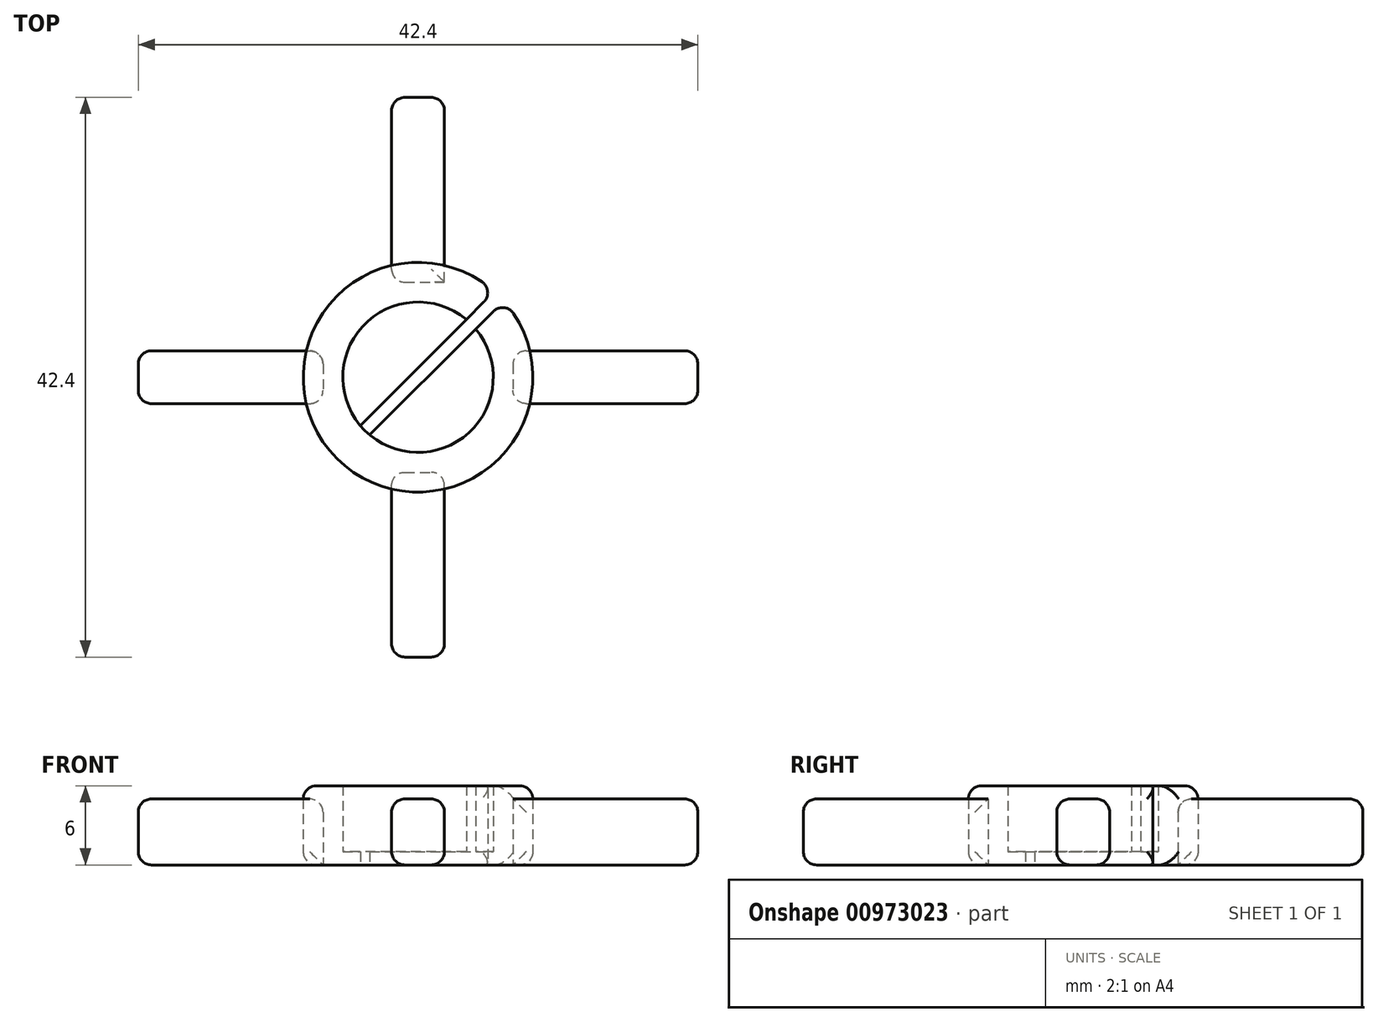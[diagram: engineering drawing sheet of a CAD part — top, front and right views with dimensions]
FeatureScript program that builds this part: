
annotation { "Feature Type Name" : "Feature", "Feature Type Description" : "" }
export const myFeature = defineFeature(function(context is Context, id is Id, definition is map)
    precondition{}
    {
        {
            var Q0;
            Q0=qCreatedBy(makeId("Top.planeOp"),FACE);
            var sketch = newSketch(context, id + "F0", { "sketchPlane" : qUnion([Q0])});
            skCircle(sketch, "E0", {"center": v(0, 0) * mm, "radius": 5.7 * mm});
            skCircle(sketch, "E1", {"center": v(0, 0) * mm, "radius": 8.7 * mm});
            skLineSegment(sketch, "E2.bottom", {"start": v(-21.2, 2) * mm, "end": v(-7.2, 2) * mm});
            skLineSegment(sketch, "E2.top", {"start": v(-21.2, -2) * mm, "end": v(-7.2, -2) * mm});
            skLineSegment(sketch, "E2.left", {"start": v(-21.2, 2) * mm, "end": v(-21.2, -2) * mm});
            skLineSegment(sketch, "E2.right", {"start": v(-7.2, 2) * mm, "end": v(-7.2, -2) * mm});
            skCircle(sketch, "E3", {"center": v(0, 0) * mm, "radius": 7.2 * mm, "construction": true});
            skPoint(sketch, "E4", {"position": v(-7.2, 0) * mm});
            skPoint(sketch, "E5", {"position": v(0, 7.2) * mm});
            skPoint(sketch, "E6", {"position": v(7.2, 0) * mm});
            skPoint(sketch, "E7", {"position": v(0, -7.2) * mm});
            skLineSegment(sketch, "E8.bottom", {"start": v(-2, 7.2) * mm, "end": v(-2, 21.2) * mm});
            skLineSegment(sketch, "E8.top", {"start": v(2, 7.2) * mm, "end": v(2, 21.2) * mm});
            skLineSegment(sketch, "E8.left", {"start": v(-2, 7.2) * mm, "end": v(2, 7.2) * mm});
            skLineSegment(sketch, "E8.right", {"start": v(-2, 21.2) * mm, "end": v(2, 21.2) * mm});
            skPoint(sketch, "E9", {"position": v(0, 21.2) * mm});
            skLineSegment(sketch, "E10.bottom", {"start": v(7.2, 2) * mm, "end": v(21.2, 2) * mm});
            skLineSegment(sketch, "E10.top", {"start": v(7.2, -2) * mm, "end": v(21.2, -2) * mm});
            skLineSegment(sketch, "E10.left", {"start": v(7.2, 2) * mm, "end": v(7.2, -2) * mm});
            skLineSegment(sketch, "E10.right", {"start": v(21.2, 2) * mm, "end": v(21.2, -2) * mm});
            skPoint(sketch, "E11", {"position": v(21.2, 0) * mm});
            skLineSegment(sketch, "E12.bottom", {"start": v(-2, -21.2) * mm, "end": v(-2, -7.2) * mm});
            skLineSegment(sketch, "E12.top", {"start": v(2, -21.2) * mm, "end": v(2, -7.2) * mm});
            skLineSegment(sketch, "E12.left", {"start": v(-2, -21.2) * mm, "end": v(2, -21.2) * mm});
            skLineSegment(sketch, "E12.right", {"start": v(-2, -7.2) * mm, "end": v(2, -7.2) * mm});
            skLineSegment(sketch, "E13.bottom", {"start": v(-0.35, 0.35) * mm, "end": v(0.35, -0.35) * mm});
            skLineSegment(sketch, "E13.top", {"start": v(13.79, 14.5) * mm, "end": v(14.5, 13.79) * mm});
            skLineSegment(sketch, "E13.left", {"start": v(-0.35, 0.35) * mm, "end": v(13.79, 14.5) * mm});
            skLineSegment(sketch, "E13.right", {"start": v(0.35, -0.35) * mm, "end": v(14.5, 13.79) * mm});
            skLineSegment(sketch, "E14", {"start": v(-0.35, 0.35) * mm, "end": v(-4.37, -3.66) * mm});
            skLineSegment(sketch, "E15", {"start": v(0.35, -0.35) * mm, "end": v(-3.66, -4.37) * mm});
            skSolve(sketch);
        }
        {
            var Q0;
            {var subQ5=sQuery(id+"F0.wireOp",EDGE,"E2.right");Q0=makeQuery(id+"F0.imprint","IMPRINT",FACE,{"disambiguationData":[TD([[makeQuery(id+"F0.imprint","IMPRINT",EDGE,{"derivedFrom":subQ5}),-1.0]])]});}
            var Q1;
            {var subQ5=sQuery(id+"F0.wireOp",EDGE,"E8.left");Q1=makeQuery(id+"F0.imprint","IMPRINT",FACE,{"disambiguationData":[TD([[makeQuery(id+"F0.imprint","IMPRINT",EDGE,{"derivedFrom":subQ5}),1.0]])]});}
            var Q2;
            {var subQ5=sQuery(id+"F0.wireOp",EDGE,"E12.left");Q2=makeQuery(id+"F0.imprint","IMPRINT",FACE,{"disambiguationData":[TD([[makeQuery(id+"F0.imprint","IMPRINT",EDGE,{"derivedFrom":subQ5}),1.0]])]});}
            var Q3;
            {var subQ5=sQuery(id+"F0.wireOp",EDGE,"E12.right");Q3=makeQuery(id+"F0.imprint","IMPRINT",FACE,{"disambiguationData":[TD([[makeQuery(id+"F0.imprint","IMPRINT",EDGE,{"derivedFrom":subQ5}),-1.0]])]});}
            var Q4;
            {var subQ5=sQuery(id+"F0.wireOp",EDGE,"E10.right");Q4=makeQuery(id+"F0.imprint","IMPRINT",FACE,{"disambiguationData":[TD([[makeQuery(id+"F0.imprint","IMPRINT",EDGE,{"derivedFrom":subQ5}),-1.0]])]});}
            var Q5;
            {var subQ5=sQuery(id+"F0.wireOp",EDGE,"E10.left");Q5=makeQuery(id+"F0.imprint","IMPRINT",FACE,{"disambiguationData":[TD([[makeQuery(id+"F0.imprint","IMPRINT",EDGE,{"derivedFrom":subQ5}),1.0]])]});}
            var Q6;
            {var subQ5=sQuery(id+"F0.wireOp",EDGE,"E2.left");Q6=makeQuery(id+"F0.imprint","IMPRINT",FACE,{"disambiguationData":[TD([[makeQuery(id+"F0.imprint","IMPRINT",EDGE,{"derivedFrom":subQ5}),1.0]])]});}
            var Q7;
            {var subQ5=sQuery(id+"F0.wireOp",EDGE,"E8.right");Q7=makeQuery(id+"F0.imprint","IMPRINT",FACE,{"disambiguationData":[TD([[makeQuery(id+"F0.imprint","IMPRINT",EDGE,{"derivedFrom":subQ5}),-1.0]])]});}
            extrude(context, id + "F1", {"entities" : qUnion([Q0, Q1, Q2, Q3, Q4, Q5, Q6, Q7]), "depth" : 5 * mm, "offsetDistance" : 25 * mm});
        }
        {
            var Q0;
            {var subQ21=sQuery(id+"F0.wireOp",EDGE,"E2.right");Q0=makeQuery(id+"F0.imprint","IMPRINT",FACE,{"disambiguationData":[TD([[makeQuery(id+"F0.imprint","IMPRINT",EDGE,{"derivedFrom":subQ21}),1.0]])]});}
            var Q1;
            {var subQ5=sQuery(id+"F0.wireOp",EDGE,"E12.right");Q1=makeQuery(id+"F0.imprint","IMPRINT",FACE,{"disambiguationData":[TD([[makeQuery(id+"F0.imprint","IMPRINT",EDGE,{"derivedFrom":subQ5}),-1.0]])]});}
            var Q2;
            {var subQ5=sQuery(id+"F0.wireOp",EDGE,"E10.left");Q2=makeQuery(id+"F0.imprint","IMPRINT",FACE,{"disambiguationData":[TD([[makeQuery(id+"F0.imprint","IMPRINT",EDGE,{"derivedFrom":subQ5}),1.0]])]});}
            var Q3;
            {var subQ5=sQuery(id+"F0.wireOp",EDGE,"E8.left");Q3=makeQuery(id+"F0.imprint","IMPRINT",FACE,{"disambiguationData":[TD([[makeQuery(id+"F0.imprint","IMPRINT",EDGE,{"derivedFrom":subQ5}),1.0]])]});}
            var Q4;
            {var subQ5=sQuery(id+"F0.wireOp",EDGE,"E2.right");Q4=makeQuery(id+"F0.imprint","IMPRINT",FACE,{"disambiguationData":[TD([[makeQuery(id+"F0.imprint","IMPRINT",EDGE,{"derivedFrom":subQ5}),-1.0]])]});}
            extrude(context, id + "F2", {"entities" : qUnion([Q0, Q1, Q2, Q3, Q4]), "depth" : 6 * mm, "offsetDistance" : 25 * mm});
        }
        {
            var Q0;
            {var subQ5=sQuery(id+"F0.wireOp",EDGE,"E13.top");Q0=makeQuery(id+"F0.imprint","IMPRINT",FACE,{"disambiguationData":[TD([[makeQuery(id+"F0.imprint","IMPRINT",EDGE,{"derivedFrom":subQ5}),-1.0]])]});}
            var Q1;
            {var subQ0=sQuery(id+"F0.wireOp",EDGE,"E13.left");var subQ1=sQuery(id+"F0.wireOp",EDGE,"E0");var subQ2=makeQuery(id+"F0.imprint","INTERSECT",VERTEX,{"derivedFrom":[subQ1,subQ0]});Q1=makeQuery(id+"F0.imprint","IMPRINT",FACE,{"disambiguationData":[TD([[makeQuery(id+"F0.imprint","IMPRINT",EDGE,{"disambiguationData":[TD([[subQ2,1.0]])],"derivedFrom":subQ1}),-1.0]])]});}
            var Q2;
            {var subQ5=sQuery(id+"F0.wireOp",EDGE,"E13.bottom");Q2=makeQuery(id+"F0.imprint","IMPRINT",FACE,{"disambiguationData":[TD([[makeQuery(id+"F0.imprint","IMPRINT",EDGE,{"derivedFrom":subQ5}),1.0]])]});}
            var Q3;
            Q3=makeQuery(id+"F0.imprint","IMPRINT",FACE,{"disambiguationData":[TD([[makeQuery(id+"F0.imprint","IMPRINT",EDGE,{"derivedFrom":sQuery(id+"F0.wireOp",EDGE,"E13.bottom")}),-1.0]])]});
            var Q4;
            Q4=makeQuery(id+"F2.opExtrude","CAP_FACE",FACE,{"disambiguationData":[OSD([sQuery(id+"F0.wireOp",EDGE,"E0"),sQuery(id+"F0.wireOp",EDGE,"E1"),sQuery(id+"F0.wireOp",EDGE,"E13.left"),sQuery(id+"F0.wireOp",EDGE,"E13.right")])],"isStart":false});
            extrude(context, id + "F3", {"entities" : qUnion([Q0, Q1, Q2, Q3]), "operationType" : NewBodyOperationType.REMOVE, "endBound" : BoundingType.UP_TO_SURFACE, "depth" : -25 * mm, "endBoundEntityFace" : qUnion([Q4]), "offsetDistance" : 25 * mm});
        }
        {
            var Q0;
            Q0=makeQuery(id+"F2.opExtrude","SWEPT_FACE",FACE,{"disambiguationData":[OSD([sQuery(id+"F0.wireOp",EDGE,"E1")])]});
            var Q1;
            Q1=makeQuery(id+"F1.opExtrude","SWEPT_FACE",FACE,{"disambiguationData":[OSD([sQuery(id+"F0.wireOp",EDGE,"E12.top")])]});
            var Q2;
            Q2=makeQuery(id+"F1.opExtrude","SWEPT_FACE",FACE,{"disambiguationData":[OSD([sQuery(id+"F0.wireOp",EDGE,"E12.bottom")])]});
            var Q3;
            Q3=makeQuery(id+"F1.opExtrude","SWEPT_FACE",FACE,{"disambiguationData":[OSD([sQuery(id+"F0.wireOp",EDGE,"E12.left")])]});
            var Q4;
            Q4=makeQuery(id+"F1.opExtrude","SWEPT_FACE",FACE,{"disambiguationData":[OSD([sQuery(id+"F0.wireOp",EDGE,"E8.bottom")])]});
            var Q5;
            Q5=makeQuery(id+"F1.opExtrude","CAP_FACE",FACE,{"disambiguationData":[OSD([sQuery(id+"F0.wireOp",EDGE,"E8.bottom"),sQuery(id+"F0.wireOp",EDGE,"E8.top"),sQuery(id+"F0.wireOp",EDGE,"E8.left"),sQuery(id+"F0.wireOp",EDGE,"E8.right")])],"isStart":false});
            var Q6;
            Q6=makeQuery(id+"F1.opExtrude","SWEPT_FACE",FACE,{"disambiguationData":[OSD([sQuery(id+"F0.wireOp",EDGE,"E8.right")])]});
            var Q7;
            Q7=makeQuery(id+"F1.opExtrude","SWEPT_FACE",FACE,{"disambiguationData":[OSD([sQuery(id+"F0.wireOp",EDGE,"E2.left")])]});
            var Q8;
            Q8=makeQuery(id+"F1.opExtrude","CAP_FACE",FACE,{"disambiguationData":[OSD([sQuery(id+"F0.wireOp",EDGE,"E2.bottom"),sQuery(id+"F0.wireOp",EDGE,"E2.top"),sQuery(id+"F0.wireOp",EDGE,"E2.left"),sQuery(id+"F0.wireOp",EDGE,"E2.right")])],"isStart":false});
            var Q9;
            Q9=makeQuery(id+"F1.opExtrude","SWEPT_FACE",FACE,{"disambiguationData":[OSD([sQuery(id+"F0.wireOp",EDGE,"E2.top")])]});
            var Q10;
            Q10=makeQuery(id+"F1.opExtrude","SWEPT_FACE",FACE,{"disambiguationData":[OSD([sQuery(id+"F0.wireOp",EDGE,"E2.bottom")])]});
            var Q11;
            Q11=makeQuery(id+"F1.opExtrude","SWEPT_FACE",FACE,{"disambiguationData":[OSD([sQuery(id+"F0.wireOp",EDGE,"E10.top")])]});
            var Q12;
            Q12=makeQuery(id+"F1.opExtrude","SWEPT_FACE",FACE,{"disambiguationData":[OSD([sQuery(id+"F0.wireOp",EDGE,"E10.right")])]});
            var Q13;
            Q13=makeQuery(id+"F1.opExtrude","SWEPT_FACE",FACE,{"disambiguationData":[OSD([sQuery(id+"F0.wireOp",EDGE,"E10.bottom")])]});
            var Q14;
            Q14=makeQuery(id+"F1.opExtrude","CAP_EDGE",EDGE,{"disambiguationData":[OSD([sQuery(id+"F0.wireOp",EDGE,"E8.top")])],"isStart":true});
            fillet(context, id + "F4", {"entities" : qUnion([Q0, Q1, Q2, Q3, Q4, Q5, Q6, Q7, Q8, Q9, Q10, Q11, Q12, Q13, Q14]), "radius" : 1 * mm, "tangentPropagation" : true, "allowEdgeOverflow" : false});
        }
        {
            var Q0;
            {var subQ0=sQuery(id+"F0.wireOp",EDGE,"E14");Q0=makeQuery(id+"F0.imprint","IMPRINT",FACE,{"disambiguationData":[TD([[makeQuery(id+"F0.imprint","IMPRINT",EDGE,{"derivedFrom":subQ0}),-1.0]])]});}
            var Q1;
            {var subQ0=sQuery(id+"F0.wireOp",EDGE,"E15");Q1=makeQuery(id+"F0.imprint","IMPRINT",FACE,{"disambiguationData":[TD([[makeQuery(id+"F0.imprint","IMPRINT",EDGE,{"derivedFrom":subQ0}),1.0]])]});}
            extrude(context, id + "F5", {"entities" : qUnion([Q0, Q1]), "operationType" : NewBodyOperationType.ADD, "depth" : 1 * mm, "offsetDistance" : 25 * mm});
        }
    });
